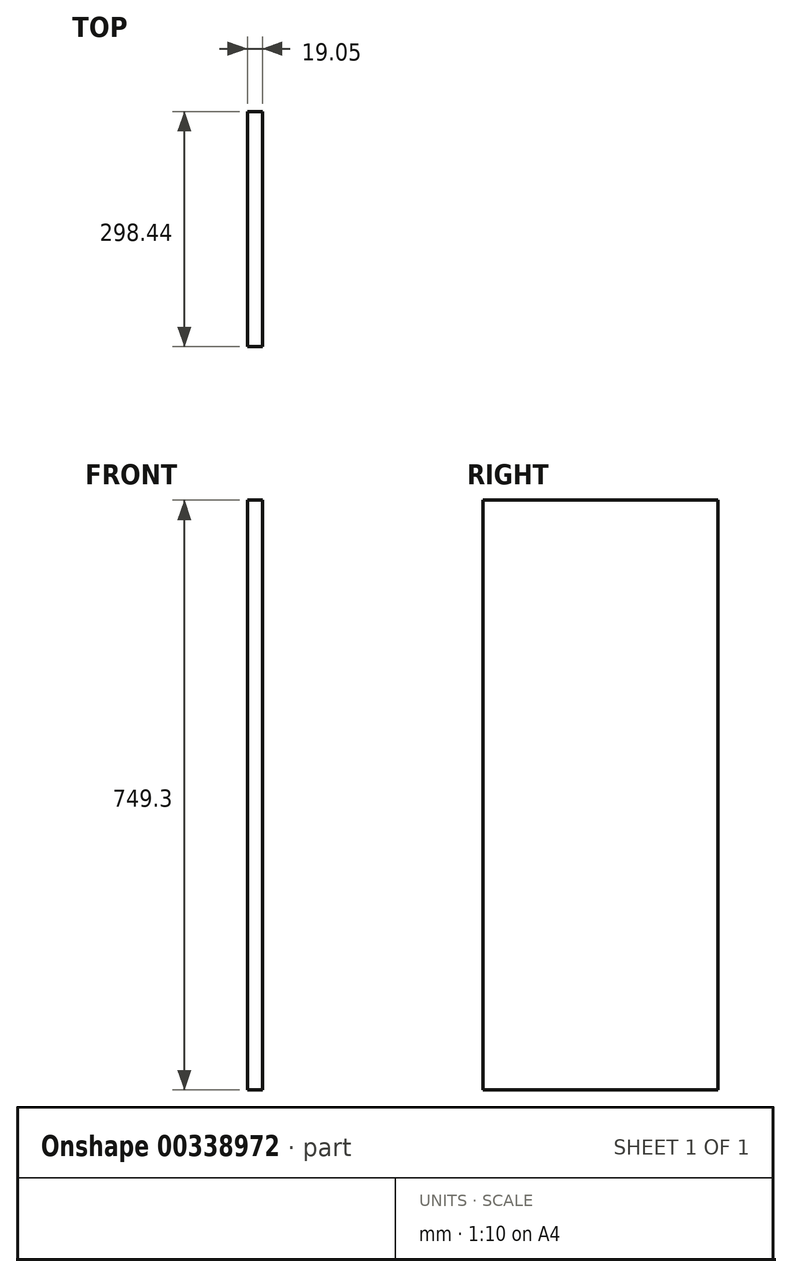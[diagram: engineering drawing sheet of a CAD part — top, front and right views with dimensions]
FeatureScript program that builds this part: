
annotation { "Feature Type Name" : "Feature", "Feature Type Description" : "" }
export const myFeature = defineFeature(function(context is Context, id is Id, definition is map)
    precondition{}
    {
        {
            var Q0;
            Q0=qCreatedBy(makeId("Right.planeOp"),FACE);
            var sketch = newSketch(context, id + "F0", { "sketchPlane" : qUnion([Q0])});
            skLineSegment(sketch, "E0.bottom", {"start": v(149.23, 374.65) * mm, "end": v(-149.22, 374.65) * mm});
            skLineSegment(sketch, "E0.top", {"start": v(149.22, -374.65) * mm, "end": v(-149.23, -374.65) * mm});
            skLineSegment(sketch, "E0.left", {"start": v(149.23, 374.65) * mm, "end": v(149.22, -374.65) * mm});
            skLineSegment(sketch, "E0.right", {"start": v(-149.22, 374.65) * mm, "end": v(-149.23, -374.65) * mm});
            skPoint(sketch, "E0.middle", {"position": v(0, 0) * mm});
            skSolve(sketch);
        }
        {
            var Q0;
            Q0 = qSketchRegion(id + "F0", true);
            extrude(context, id + "F1", {"entities" : qUnion([Q0]), "depth" : 19.05 * mm});
        }
    });
